# Revit family: MH-X00
name_source: partatom
category: Plumbing Fixtures
units: mm (PartAtom-declared; Revit-internal decimal feet)

## family parameters
Always vertical = No
Cut with Voids When Loaded = No
OmniClass Number = 23.70.50.21.24.11
OmniClass Title = Roof Waste Water Drains
Part Type = Normal
Room Calculation Point = No
Round Connector Dimension = Use Diameter
Shared = No
Work Plane-Based = Yes

## types (5) — shared parameters
Default Elevation = 48"
EE3 = 7/8"
G2 = 1/8"
HH2 = 1/8"
II1 = 1/8"
II2 = 1/8"
Manufacturer = MIFAB

MIFAB
MIFAB
R1 = 1/4"
RP2 = 1/4"
SC1 = 1/8"
SC2 = 1/8"
URL = www.mifab.com
id1 = 1/4"
id3 = 1/8"
od3 = 1/4"
r2 = 3/4"

## per-type parameters (varying)
- MH-500: A=19 3/8"; A'=9 5/8"; B=17 7/8"; B'=8 7/8"; B01=8 1/2"; C=12 1/4"; C'=6 1/8"; C'1=6 1/2"; Connection Dia=0"; D=4 3/8"; Description=5" HydroMax Siphonic Roof Drain; EE=7 7/8"; EE1=2 5/8"; EE2=3 1/4"; FF=0"; G1=6 3/8"; HH1=3 1/8"; PIPE SIZE=4 7/8"; PIPE SIZE'=2 1/2"; RP1=1/4"; V1=Yes; V2=No; V3=Yes; V4=Yes; V5=Yes; V6=No; ff2=2 3/4"; linearL=1 7/8"; linearW=3 7/8"; od1=1/2"; od2=3/8"
- MH-300: A=13"; A'=6 1/2"; B=11 3/4"; B'=5 7/8"; B01=5 1/2"; C=7 1/4"; C'=3 5/8"; C'1=4"; Connection Dia=2 1/2"; D=3 1/8"; Description=3" HydroMax Siphonic Roof Drain; EE=3 3/4"; EE1=2 7/8"; EE2=3 1/4"; FF=0"; G1=3"; HH1=3 1/8"; PIPE SIZE=3"; PIPE SIZE'=1 1/2"; RP1=1/8"; V1=Yes; V2=No; V3=Yes; V4=Yes; V5=No; V6=No; ff2=2 3/4"; linearL=1"; linearW=2 1/8"; od1=3/8"; od2=3/8"
- MH-400: A=19 3/8"; A'=9 5/8"; B=17 7/8"; B'=8 7/8"; B01=8 1/2"; C=10 5/8"; C'=5 3/8"; C'1=5 3/4"; Connection Dia=0"; D=3 1/2"; Description=4" HydroMax Siphonic Roof Drain; EE=7 7/8"; EE1=2 5/8"; EE2=3 1/4"; FF=0"; G1=6 3/8"; HH1=3 1/8"; PIPE SIZE=3 7/8"; PIPE SIZE'=2"; RP1=1/8"; V1=Yes; V2=No; V3=Yes; V4=Yes; V5=Yes; V6=No; ff2=2 3/4"; linearL=1 5/8"; linearW=3 1/2"; od1=3/8"; od2=3/8"
- MH-600: A=25 1/4"; A'=12 5/8"; B=22 1/4"; B'=11 1/8"; B01=10 5/8"; C=15 1/2"; C'=7 3/4"; C'1=8 1/4"; Connection Dia=0"; D=4 3/4"; Description=6" HydroMax Siphonic Roof Drain; EE=7 7/8"; EE1=2 5/8"; EE2=3 1/4"; FF=0"; G1=6 3/8"; HH1=3 1/8"; PIPE SIZE=5 7/8"; PIPE SIZE'=3"; RP1=1/4"; V1=Yes; V2=Yes; V3=Yes; V4=Yes; V5=Yes; V6=No; ff2=2 3/4"; linearL=2 1/2"; linearW=5 1/2"; od1=1/2"; od2=1/2"
- MH-200: A=13"; A'=6 1/2"; B=11 3/4"; B'=5 7/8"; B01=5 1/2"; C=7 1/4"; C'=3 5/8"; C'1=4"; Connection Dia=0"; D=3 1/8"; Description=2" HydroMax Siphonic Roof Drain; EE=2 1/2"; EE1=2 1/8"; EE2=2 3/8"; FF=3/8"; G1=2"; HH1=1 3/4"; PIPE SIZE=3"; PIPE SIZE'=1 1/2"; RP1=1/8"; V1=No; V2=No; V3=No; V4=No; V5=No; V6=Yes; ff2=2"; linearL=1"; linearW=2 1/8"; od1=3/8"; od2=3/8"

note: column(s) folded — value = type name in every type: Model

## geometry (parser evidence)
native form markers: Sweep x3
no freeform markers — native parametric forms only
